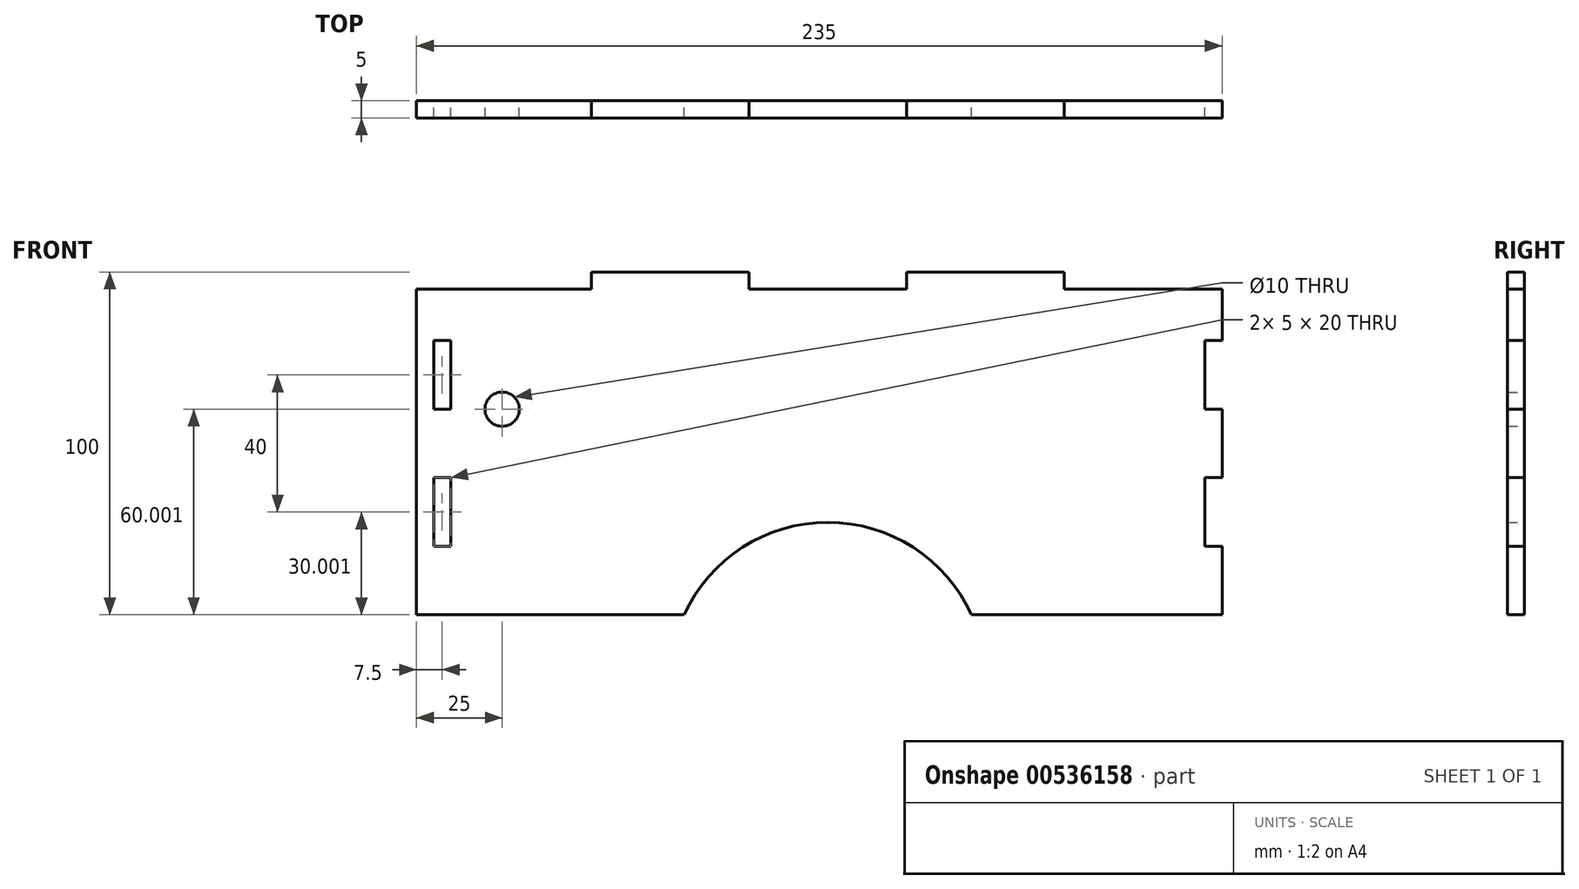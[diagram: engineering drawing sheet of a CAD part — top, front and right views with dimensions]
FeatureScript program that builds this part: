
annotation { "Feature Type Name" : "Feature", "Feature Type Description" : "" }
export const myFeature = defineFeature(function(context is Context, id is Id, definition is map)
    precondition{}
    {
        {
            var Q0;
            Q0=qCreatedBy(makeId("Front.planeOp"),FACE);
            var sketch = newSketch(context, id + "F0", { "sketchPlane" : qUnion([Q0])});
            skLineSegment(sketch, "E0.top", {"start": v(110, -49.1) * mm, "end": v(41.9, -49.1) * mm});
            skLineSegment(sketch, "E0.left", {"start": v(110, 30.9) * mm, "end": v(110, 10.9) * mm});
            skLineSegment(sketch, "E0.right", {"start": v(-110, 30.9) * mm, "end": v(-110, 10.9) * mm});
            skPoint(sketch, "E0.middle", {"position": v(0, -1.6) * mm});
            skLineSegment(sketch, "E1", {"start": v(-115, -29.1) * mm, "end": v(-115, -9.1) * mm, "construction": true});
            skLineSegment(sketch, "E2", {"start": v(-69, 50.9) * mm, "end": v(-23, 50.9) * mm, "construction": true});
            skLineSegment(sketch, "E3", {"start": v(115, 45.9) * mm, "end": v(115, -49.1) * mm, "construction": true});
            skArc(sketch, "E4", {"start": v(41.9, -49.1) * mm, "mid": v(0, -22.1) * mm, "end": v(-41.9, -49.1) * mm});
            skLineSegment(sketch, "E5.bottom", {"start": v(-110, -49.1) * mm, "end": v(-41.9, -49.1) * mm, "construction": true});
            skLineSegment(sketch, "E5.top", {"start": v(-110, -134.1) * mm, "end": v(110, -134.1) * mm, "construction": true});
            skLineSegment(sketch, "E5.left", {"start": v(-110, -49.1) * mm, "end": v(-110, -134.1) * mm, "construction": true});
            skLineSegment(sketch, "E5.right", {"start": v(110, -49.1) * mm, "end": v(110, -134.1) * mm, "construction": true});
            skLineSegment(sketch, "E6.trimOffspring", {"start": v(41.9, -49.1) * mm, "end": v(110, -49.1) * mm, "construction": true});
            skLineSegment(sketch, "E7.trimOffspring", {"start": v(-41.9, -49.1) * mm, "end": v(-110, -49.1) * mm});
            skLineSegment(sketch, "E8", {"start": v(-110, -49.1) * mm, "end": v(-115, -49.1) * mm});
            skLineSegment(sketch, "E9", {"start": v(-115, -29.1) * mm, "end": v(-110, -29.1) * mm});
            skLineSegment(sketch, "E10", {"start": v(-110, -9.1) * mm, "end": v(-115, -9.1) * mm});
            skLineSegment(sketch, "E11", {"start": v(-115, 10.9) * mm, "end": v(-110, 10.9) * mm});
            skLineSegment(sketch, "E12", {"start": v(-110, 30.9) * mm, "end": v(-115, 30.9) * mm});
            skLineSegment(sketch, "E13", {"start": v(-69, 50.9) * mm, "end": v(-69, 45.9) * mm});
            skLineSegment(sketch, "E14.trimOffspring", {"start": v(-110, -9.1) * mm, "end": v(-110, -19.1) * mm});
            skPoint(sketch, "E15.orphan", {"position": v(-110, 45.9) * mm});
            skLineSegment(sketch, "E16", {"start": v(-23, 45.9) * mm, "end": v(-23, 50.9) * mm});
            skLineSegment(sketch, "E17.MirrorCS", {"start": v(110, -49.1) * mm, "end": v(115, -49.1) * mm});
            skLineSegment(sketch, "E18.MirrorCS", {"start": v(115, -29.1) * mm, "end": v(110, -29.1) * mm});
            skLineSegment(sketch, "E19.MirrorCS", {"start": v(110, -9.1) * mm, "end": v(115, -9.1) * mm});
            skLineSegment(sketch, "E20.MirrorCS", {"start": v(115, 10.9) * mm, "end": v(110, 10.9) * mm});
            skLineSegment(sketch, "E21.MirrorCS", {"start": v(110, 30.9) * mm, "end": v(115, 30.9) * mm});
            skLineSegment(sketch, "E22.MirrorCS", {"start": v(23, 45.9) * mm, "end": v(23, 50.9) * mm});
            skLineSegment(sketch, "E23.MirrorCS", {"start": v(69, 50.9) * mm, "end": v(69, 45.9) * mm});
            skLineSegment(sketch, "E24", {"start": v(115, 45.9) * mm, "end": v(115, 30.9) * mm});
            skLineSegment(sketch, "E25", {"start": v(115, 10.9) * mm, "end": v(115, -9.1) * mm});
            skPoint(sketch, "E26.orphan", {"position": v(110, 45.9) * mm});
            skLineSegment(sketch, "E27.trimOffspring", {"start": v(110, -9.1) * mm, "end": v(110, -29.1) * mm});
            skLineSegment(sketch, "E28", {"start": v(115, -29.1) * mm, "end": v(115, -49.1) * mm});
            skLineSegment(sketch, "E29", {"start": v(-69, 45.9) * mm, "end": v(-115, 45.9) * mm});
            skLineSegment(sketch, "E30", {"start": v(-69, 50.9) * mm, "end": v(-23, 50.9) * mm});
            skLineSegment(sketch, "E31.trimOffspring", {"start": v(23, 50.9) * mm, "end": v(69, 50.9) * mm, "construction": true});
            skLineSegment(sketch, "E32", {"start": v(-23, 45.9) * mm, "end": v(23, 45.9) * mm});
            skLineSegment(sketch, "E33", {"start": v(23, 50.9) * mm, "end": v(69, 50.9) * mm});
            skLineSegment(sketch, "E34", {"start": v(115, 45.9) * mm, "end": v(69, 45.9) * mm});
            skLineSegment(sketch, "E35.bottom", {"start": v(-115, 45.9) * mm, "end": v(-120, 45.9) * mm});
            skLineSegment(sketch, "E35.top", {"start": v(-115, -49.1) * mm, "end": v(-120, -49.1) * mm});
            skLineSegment(sketch, "E35.left", {"start": v(-115, 30.9) * mm, "end": v(-115, 10.9) * mm});
            skLineSegment(sketch, "E35.right", {"start": v(-120, 45.9) * mm, "end": v(-120, -49.1) * mm});
            skLineSegment(sketch, "E36.trimOffspring", {"start": v(-115, 10.9) * mm, "end": v(-115, 30.9) * mm, "construction": true});
            skLineSegment(sketch, "E37.trimOffspring", {"start": v(-115, -9.1) * mm, "end": v(-115, -29.1) * mm});
            skLineSegment(sketch, "E38", {"start": v(-110, -29.1) * mm, "end": v(-110, -19.1) * mm});
            skCircle(sketch, "E39", {"center": v(-95, 10.9) * mm, "radius": 5 * mm});
            skSolve(sketch);
        }
        {
            var Q0;
            Q0 = qSketchRegion(id + "F0", true);
            extrude(context, id + "F1", {"entities" : qUnion([Q0]), "depth" : 5 * mm, "offsetDistance" : 25 * mm});
        }
    });
